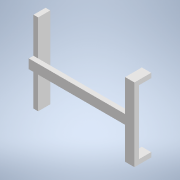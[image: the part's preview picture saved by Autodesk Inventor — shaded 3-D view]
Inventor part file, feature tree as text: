
AUTODESK INVENTOR PART (.ipt)
format: ipt  version: 2020 (Build 240168000, 168)  size: 139,264 bytes
history: native  units: in
note: dims shown in document units (in); Inventor stores cm internally (conversion verified against a paired STEP export)
features: reference x6, sketch x4, extrude x3, other x2
ambient origin geometry x8: Origin, YZ Plane, XZ Plane, XY Plane, X Axis, Y Axis, Z Axis, Center Point
bodies: Solid1 (feature_tree)
feature tree (15):
  sketch  "Sketch1"  dims[d0=0.1969in d1=0.1969in]
  extrude  "Extrusion1"  Depth=0.1969in
  extrude  "Extrusion2"  Depth=0.3937in
  extrude  "Extrusion3"  Depth=0.3937in
  sketch  "Sketch2"  dims[d2=0.1969in d3=0.3937in]
  reference  "Reference1"
  reference  "Reference2"
  reference  "Reference3"
  reference  "Reference4"
  reference  "Reference5"
  sketch  "Sketch3"  dims[d5=0.3937in d6=0.3937in]
  reference  "Reference6"
  sketch  "Sketch4"  dims[d7=0.1969in d8=0.0in d9=0.5094in d10=0.0in d11=0.1969in d12=0.0in]
  other  "Assembly1"
  other  "galaxy s8 dimensions:1"
